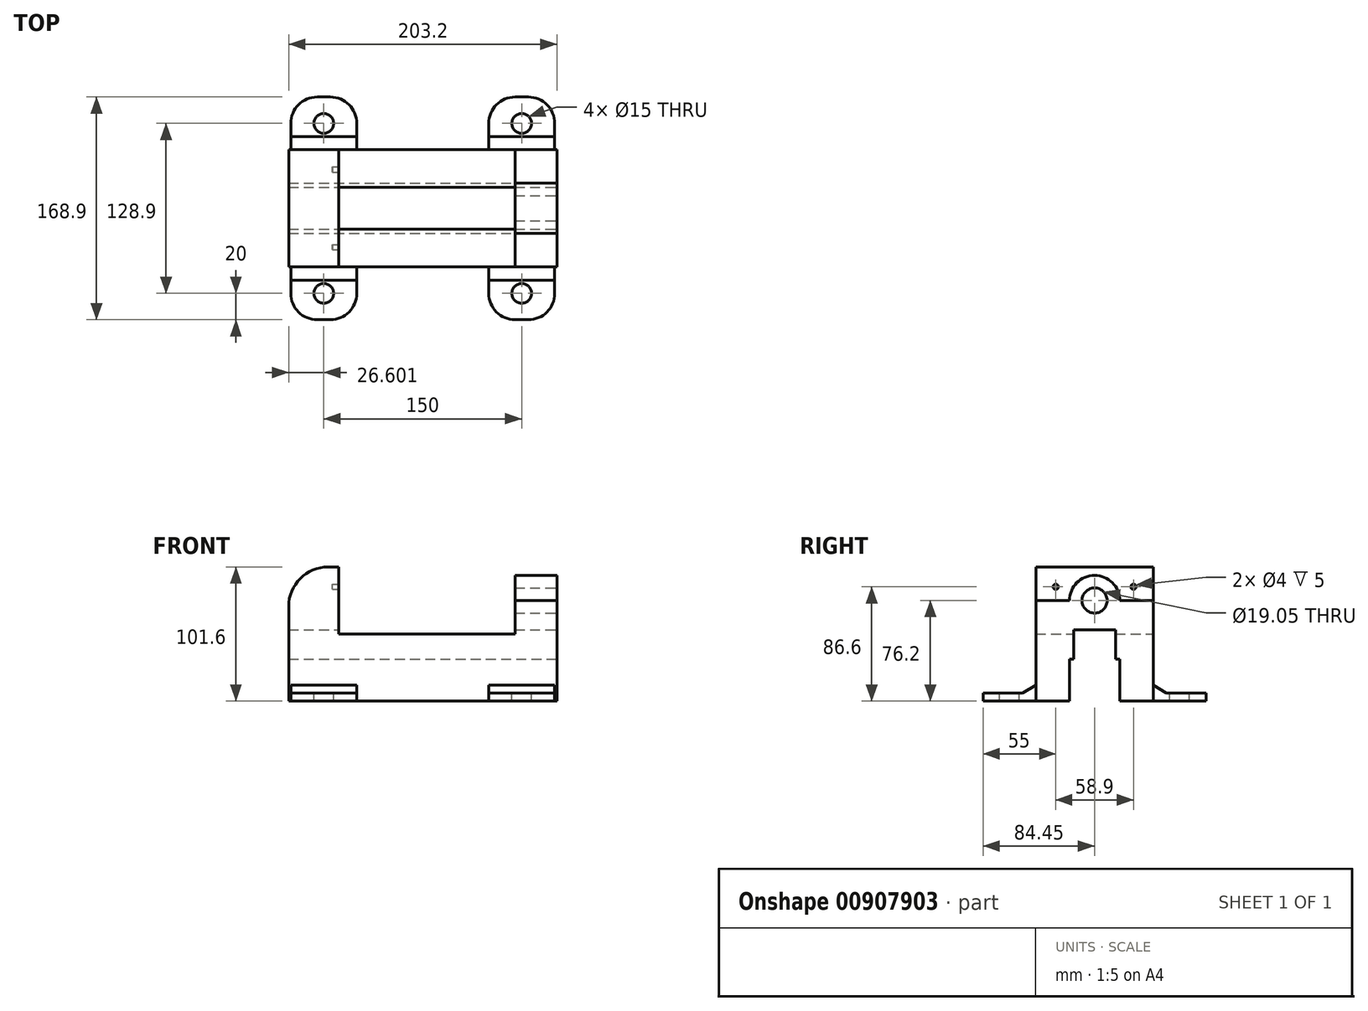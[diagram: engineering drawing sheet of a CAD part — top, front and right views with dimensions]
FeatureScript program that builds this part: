
annotation { "Feature Type Name" : "Feature", "Feature Type Description" : "" }
export const myFeature = defineFeature(function(context is Context, id is Id, definition is map)
    precondition{}
    {
        {
            var Q0;
            Q0=qCreatedBy(makeId("Front.planeOp"),FACE);
            var sketch = newSketch(context, id + "F0", { "sketchPlane" : qUnion([Q0])});
            skLineSegment(sketch, "E0", {"start": v(-86.38, 0) * mm, "end": v(116.82, 0) * mm});
            skLineSegment(sketch, "E1", {"start": v(116.82, 0) * mm, "end": v(116.82, 76.2) * mm});
            skLineSegment(sketch, "E2", {"start": v(116.82, 76.2) * mm, "end": v(85.07, 76.2) * mm});
            skLineSegment(sketch, "E3", {"start": v(85.07, 76.2) * mm, "end": v(85.07, 50.8) * mm});
            skLineSegment(sketch, "E4", {"start": v(85.07, 50.8) * mm, "end": v(-48.28, 50.8) * mm});
            skLineSegment(sketch, "E5", {"start": v(-48.28, 50.8) * mm, "end": v(-48.28, 101.6) * mm});
            skLineSegment(sketch, "E6", {"start": v(-48.28, 101.6) * mm, "end": v(-86.38, 101.6) * mm});
            skLineSegment(sketch, "E7", {"start": v(-86.38, 101.6) * mm, "end": v(-86.38, 0) * mm});
            skSolve(sketch);
        }
        {
            var Q0;
            Q0=makeQuery(id+"F0.imprint","IMPRINT",FACE,{"disambiguationData":[TD([[makeQuery(id+"F0.imprint","IMPRINT",EDGE,{"derivedFrom":sQuery(id+"F0.wireOp",EDGE,"E0")}),1.0]])]});
            extrude(context, id + "F1", {"entities" : qUnion([Q0]), "depth" : 88.9 * mm, "offsetDistance" : 25 * mm});
        }
        {
            var Q0;
            Q0=makeQuery(id+"F1.opExtrude","SWEPT_EDGE",EDGE,{"disambiguationData":[OSD([sQuery(id+"F0.wireOp",EDGE,"E6"),sQuery(id+"F0.wireOp",EDGE,"E7")])]});
            fillet(context, id + "F2", {"entities" : qUnion([Q0]), "radius" : 30 * mm, "tangentPropagation" : true, "allowEdgeOverflow" : false});
        }
        {
            var Q0;
            Q0=makeQuery(id+"F1.opExtrude","SWEPT_FACE",FACE,{"disambiguationData":[OSD([sQuery(id+"F0.wireOp",EDGE,"E1")])]});
            var sketch = newSketch(context, id + "F3", { "sketchPlane" : qUnion([Q0])});
            skCircle(sketch, "E8", {"center": v(-44.45, 76.2) * mm, "radius": 19.05 * mm});
            skSolve(sketch);
        }
        {
            var Q0;
            {var subQ0=sQuery(id+"F3.wireOp",EDGE,"E8");var subQ1=makeQuery(id+"F1.opExtrude","SWEPT_EDGE",EDGE,{"disambiguationData":[OSD([sQuery(id+"F0.wireOp",EDGE,"E1"),sQuery(id+"F0.wireOp",EDGE,"E2")])]});var subQ2=makeQuery(id+"F3.imprint","INTERSECT",VERTEX,{"disambiguationData":[OD(0.0)],"derivedFrom":[subQ1,subQ0]});Q0=makeQuery(id+"F3.imprint","IMPRINT",FACE,{"disambiguationData":[TD([[makeQuery(id+"F3.imprint","IMPRINT",EDGE,{"disambiguationData":[TD([[subQ2,-1.0]])],"derivedFrom":subQ0}),1.0]])]});}
            extrude(context, id + "F4", {"entities" : qUnion([Q0]), "operationType" : NewBodyOperationType.ADD, "oppositeDirection" : true, "depth" : 31.75 * mm, "offsetDistance" : 25 * mm});
        }
        {
            var Q0;
            {var subQ0=sQuery(id+"F0.wireOp",EDGE,"E1");Q0=makeQuery(id+"F4.boolean.opBoolean","MERGE",FACE,{"derivedFrom":[makeQuery(id+"F1.opExtrude","SWEPT_FACE",FACE,{"disambiguationData":[OSD([subQ0])]}),makeQuery(id+"F4.opExtrude","CAP_FACE",FACE,{"disambiguationData":[OSD([subQ0,sQuery(id+"F0.wireOp",EDGE,"E2"),sQuery(id+"F3.wireOp",EDGE,"E8")])],"isStart":true})]});}
            var sketch = newSketch(context, id + "F5", { "sketchPlane" : qUnion([Q0])});
            skCircle(sketch, "E9", {"center": v(-44.45, 76.2) * mm, "radius": 19.05 * mm});
            skCircle(sketch, "E10", {"center": v(-44.45, 76.2) * mm, "radius": 7.94 * mm});
            skSolve(sketch);
        }
        {
            var Q0;
            Q0=makeQuery(id+"F5.imprint","IMPRINT",FACE,{"disambiguationData":[TD([[makeQuery(id+"F5.imprint","IMPRINT",EDGE,{"derivedFrom":sQuery(id+"F5.wireOp",EDGE,"E10")}),1.0]])]});
            extrude(context, id + "F6", {"entities" : qUnion([Q0]), "operationType" : NewBodyOperationType.REMOVE, "oppositeDirection" : true, "depth" : 55 * mm, "offsetDistance" : 25 * mm});
        }
        {
            var Q0;
            {var subQ0=sQuery(id+"F0.wireOp",EDGE,"E1");Q0=makeQuery(id+"F4.boolean.opBoolean","MERGE",FACE,{"derivedFrom":[makeQuery(id+"F1.opExtrude","SWEPT_FACE",FACE,{"disambiguationData":[OSD([subQ0])]}),makeQuery(id+"F4.opExtrude","CAP_FACE",FACE,{"disambiguationData":[OSD([subQ0,sQuery(id+"F0.wireOp",EDGE,"E2"),sQuery(id+"F3.wireOp",EDGE,"E8")])],"isStart":true})]});}
            var sketch = newSketch(context, id + "F7", { "sketchPlane" : qUnion([Q0])});
            skLineSegment(sketch, "E11", {"start": v(-44.45, 0) * mm, "end": v(-63.5, 0) * mm});
            skLineSegment(sketch, "E12", {"start": v(-63.5, 0) * mm, "end": v(-25.4, 0) * mm});
            skLineSegment(sketch, "E13", {"start": v(-25.4, 0) * mm, "end": v(-25.4, 31.75) * mm});
            skLineSegment(sketch, "E14", {"start": v(-25.4, 31.75) * mm, "end": v(-63.5, 31.75) * mm});
            skLineSegment(sketch, "E15", {"start": v(-63.5, 31.75) * mm, "end": v(-63.5, 0) * mm});
            skLineSegment(sketch, "E16", {"start": v(-44.45, 31.75) * mm, "end": v(-44.45, 53.98) * mm});
            skLineSegment(sketch, "E17", {"start": v(-44.45, 53.98) * mm, "end": v(-60.33, 53.98) * mm});
            skLineSegment(sketch, "E18", {"start": v(-60.33, 53.98) * mm, "end": v(-60.33, 31.75) * mm});
            skLineSegment(sketch, "E19", {"start": v(-60.33, 31.75) * mm, "end": v(-28.57, 31.75) * mm});
            skLineSegment(sketch, "E20", {"start": v(-28.57, 31.75) * mm, "end": v(-28.57, 53.98) * mm});
            skLineSegment(sketch, "E21", {"start": v(-28.57, 53.98) * mm, "end": v(-44.45, 53.98) * mm});
            skSolve(sketch);
        }
        {
            var Q0;
            {var subQ4=sQuery(id+"F7.wireOp",EDGE,"E13");Q0=makeQuery(id+"F7.imprint","IMPRINT",FACE,{"disambiguationData":[TD([[makeQuery(id+"F7.imprint","IMPRINT",EDGE,{"derivedFrom":subQ4}),1.0]])]});}
            var Q1;
            {var subQ0=sQuery(id+"F7.wireOp",EDGE,"E16");Q1=makeQuery(id+"F7.imprint","IMPRINT",FACE,{"disambiguationData":[TD([[makeQuery(id+"F7.imprint","IMPRINT",EDGE,{"derivedFrom":subQ0}),1.0]])]});}
            var Q2;
            {var subQ0=sQuery(id+"F7.wireOp",EDGE,"E16");Q2=makeQuery(id+"F7.imprint","IMPRINT",FACE,{"disambiguationData":[TD([[makeQuery(id+"F7.imprint","IMPRINT",EDGE,{"derivedFrom":subQ0}),-1.0]])]});}
            extrude(context, id + "F8", {"entities" : qUnion([Q0, Q1, Q2]), "operationType" : NewBodyOperationType.REMOVE, "oppositeDirection" : true, "depth" : 265 * mm, "offsetDistance" : 25 * mm});
        }
        {
            var Q0;
            Q0=makeQuery(id+"F1.opExtrude","CAP_FACE",FACE,{"disambiguationData":[OSD([sQuery(id+"F0.wireOp",EDGE,"E0"),sQuery(id+"F0.wireOp",EDGE,"E1"),sQuery(id+"F0.wireOp",EDGE,"E2"),sQuery(id+"F0.wireOp",EDGE,"E3"),sQuery(id+"F0.wireOp",EDGE,"E4"),sQuery(id+"F0.wireOp",EDGE,"E5"),sQuery(id+"F0.wireOp",EDGE,"E6"),sQuery(id+"F0.wireOp",EDGE,"E7")])],"isStart":false});
            var sketch = newSketch(context, id + "F9", { "sketchPlane" : qUnion([Q0])});
            skLineSegment(sketch, "E22", {"start": v(-86.38, 0) * mm, "end": v(-84.78, 0) * mm});
            skLineSegment(sketch, "E23", {"start": v(-84.78, 0) * mm, "end": v(-84.78, 6) * mm});
            skLineSegment(sketch, "E24", {"start": v(-84.78, 6) * mm, "end": v(-34.78, 6) * mm});
            skLineSegment(sketch, "E25", {"start": v(-34.78, 6) * mm, "end": v(-34.78, 0) * mm});
            skLineSegment(sketch, "E26", {"start": v(-34.78, 0) * mm, "end": v(-84.78, 0) * mm});
            skLineSegment(sketch, "E27", {"start": v(116.82, 0) * mm, "end": v(115.22, 0) * mm});
            skLineSegment(sketch, "E28", {"start": v(115.22, 0) * mm, "end": v(115.22, 6) * mm});
            skLineSegment(sketch, "E29", {"start": v(115.22, 6) * mm, "end": v(65.22, 6) * mm});
            skLineSegment(sketch, "E30", {"start": v(65.22, 6) * mm, "end": v(65.22, 0) * mm});
            skLineSegment(sketch, "E31", {"start": v(65.22, 0) * mm, "end": v(115.22, 0) * mm});
            skSolve(sketch);
        }
        {
            var Q0;
            Q0=makeQuery(id+"F9.imprint","IMPRINT",FACE,{"disambiguationData":[TD([[makeQuery(id+"F9.imprint","IMPRINT",EDGE,{"derivedFrom":sQuery(id+"F9.wireOp",EDGE,"E23")}),-1.0]])]});
            var Q1;
            Q1=makeQuery(id+"F9.imprint","IMPRINT",FACE,{"disambiguationData":[TD([[makeQuery(id+"F9.imprint","IMPRINT",EDGE,{"derivedFrom":sQuery(id+"F9.wireOp",EDGE,"E28")}),1.0]])]});
            extrude(context, id + "F10", {"entities" : qUnion([Q0, Q1]), "operationType" : NewBodyOperationType.ADD, "depth" : 40 * mm, "offsetDistance" : 25 * mm});
        }
        {
            var Q0;
            Q0=makeQuery(id+"F10.opExtrude","CAP_EDGE",EDGE,{"disambiguationData":[OSD([sQuery(id+"F9.wireOp",EDGE,"E23")])],"isStart":false});
            var Q1;
            Q1=makeQuery(id+"F10.opExtrude","CAP_EDGE",EDGE,{"disambiguationData":[OSD([sQuery(id+"F9.wireOp",EDGE,"E25")])],"isStart":false});
            var Q2;
            Q2=makeQuery(id+"F10.opExtrude","CAP_EDGE",EDGE,{"disambiguationData":[OSD([sQuery(id+"F9.wireOp",EDGE,"E30")])],"isStart":false});
            var Q3;
            Q3=makeQuery(id+"F10.opExtrude","CAP_EDGE",EDGE,{"disambiguationData":[OSD([sQuery(id+"F9.wireOp",EDGE,"E28")])],"isStart":false});
            fillet(context, id + "F11", {"entities" : qUnion([Q0, Q1, Q2, Q3]), "radius" : 20 * mm, "tangentPropagation" : true, "allowEdgeOverflow" : false});
        }
        {
            var Q0;
            Q0=makeQuery(id+"F1.opExtrude","CAP_FACE",FACE,{"disambiguationData":[OSD([sQuery(id+"F0.wireOp",EDGE,"E0"),sQuery(id+"F0.wireOp",EDGE,"E1"),sQuery(id+"F0.wireOp",EDGE,"E2"),sQuery(id+"F0.wireOp",EDGE,"E3"),sQuery(id+"F0.wireOp",EDGE,"E4"),sQuery(id+"F0.wireOp",EDGE,"E5"),sQuery(id+"F0.wireOp",EDGE,"E6"),sQuery(id+"F0.wireOp",EDGE,"E7")])],"isStart":true});
            var sketch = newSketch(context, id + "F12", { "sketchPlane" : qUnion([Q0])});
            skLineSegment(sketch, "E32", {"start": v(-116.82, 0) * mm, "end": v(-115.22, 0) * mm});
            skLineSegment(sketch, "E33", {"start": v(-115.22, 0) * mm, "end": v(-115.22, 6) * mm});
            skLineSegment(sketch, "E34", {"start": v(-115.22, 6) * mm, "end": v(-65.22, 6) * mm});
            skLineSegment(sketch, "E35", {"start": v(-65.22, 6) * mm, "end": v(-65.22, 0) * mm});
            skLineSegment(sketch, "E36", {"start": v(-65.22, 0) * mm, "end": v(-115.22, 0) * mm});
            skLineSegment(sketch, "E37", {"start": v(86.38, 0) * mm, "end": v(84.78, 0) * mm});
            skLineSegment(sketch, "E38", {"start": v(84.78, 0) * mm, "end": v(84.78, 6) * mm});
            skLineSegment(sketch, "E39", {"start": v(84.78, 6) * mm, "end": v(34.78, 6) * mm});
            skLineSegment(sketch, "E40", {"start": v(34.78, 6) * mm, "end": v(34.78, 0) * mm});
            skLineSegment(sketch, "E41", {"start": v(34.78, 0) * mm, "end": v(84.78, 0) * mm});
            skSolve(sketch);
        }
        {
            var Q0;
            Q0=makeQuery(id+"F12.imprint","IMPRINT",FACE,{"disambiguationData":[TD([[makeQuery(id+"F12.imprint","IMPRINT",EDGE,{"derivedFrom":sQuery(id+"F12.wireOp",EDGE,"E33")}),-1.0]])]});
            var Q1;
            Q1=makeQuery(id+"F12.imprint","IMPRINT",FACE,{"disambiguationData":[TD([[makeQuery(id+"F12.imprint","IMPRINT",EDGE,{"derivedFrom":sQuery(id+"F12.wireOp",EDGE,"E38")}),1.0]])]});
            extrude(context, id + "F13", {"entities" : qUnion([Q0, Q1]), "operationType" : NewBodyOperationType.ADD, "depth" : 40 * mm, "offsetDistance" : 25 * mm});
        }
        {
            var Q0;
            Q0=makeQuery(id+"F13.opExtrude","CAP_EDGE",EDGE,{"disambiguationData":[OSD([sQuery(id+"F12.wireOp",EDGE,"E33")])],"isStart":false});
            var Q1;
            Q1=makeQuery(id+"F13.opExtrude","CAP_EDGE",EDGE,{"disambiguationData":[OSD([sQuery(id+"F12.wireOp",EDGE,"E35")])],"isStart":false});
            var Q2;
            Q2=makeQuery(id+"F13.opExtrude","CAP_EDGE",EDGE,{"disambiguationData":[OSD([sQuery(id+"F12.wireOp",EDGE,"E40")])],"isStart":false});
            var Q3;
            Q3=makeQuery(id+"F13.opExtrude","CAP_EDGE",EDGE,{"disambiguationData":[OSD([sQuery(id+"F12.wireOp",EDGE,"E38")])],"isStart":false});
            fillet(context, id + "F14", {"entities" : qUnion([Q0, Q1, Q2, Q3]), "radius" : 20 * mm, "tangentPropagation" : true, "allowEdgeOverflow" : false});
        }
        {
            var Q0;
            Q0=makeQuery(id+"F13.opExtrude","SWEPT_FACE",FACE,{"disambiguationData":[OSD([sQuery(id+"F12.wireOp",EDGE,"E34")])]});
            var sketch = newSketch(context, id + "F15", { "sketchPlane" : qUnion([Q0])});
            skLineSegment(sketch, "E42", {"start": v(90.22, 40) * mm, "end": v(90.22, 20) * mm});
            skCircle(sketch, "E43", {"center": v(90.22, 20) * mm, "radius": 7.5 * mm});
            skSolve(sketch);
        }
        {
            var Q0;
            Q0=makeQuery(id+"F15.imprint","IMPRINT",FACE,{"disambiguationData":[TD([[makeQuery(id+"F15.imprint","IMPRINT",EDGE,{"derivedFrom":sQuery(id+"F15.wireOp",EDGE,"E43")}),1.0]])]});
            extrude(context, id + "F16", {"entities" : qUnion([Q0]), "operationType" : NewBodyOperationType.REMOVE, "oppositeDirection" : true, "depth" : 25 * mm, "offsetDistance" : 25 * mm});
        }
        {
            var Q0;
            Q0=makeQuery(id+"F13.opExtrude","SWEPT_FACE",FACE,{"disambiguationData":[OSD([sQuery(id+"F12.wireOp",EDGE,"E39")])]});
            var sketch = newSketch(context, id + "F17", { "sketchPlane" : qUnion([Q0])});
            skLineSegment(sketch, "E44", {"start": v(-59.78, 40) * mm, "end": v(-59.78, 20) * mm});
            skCircle(sketch, "E45", {"center": v(-59.78, 20) * mm, "radius": 7.5 * mm});
            skSolve(sketch);
        }
        {
            var Q0;
            Q0=makeQuery(id+"F17.imprint","IMPRINT",FACE,{"disambiguationData":[TD([[makeQuery(id+"F17.imprint","IMPRINT",EDGE,{"derivedFrom":sQuery(id+"F17.wireOp",EDGE,"E45")}),1.0]])]});
            extrude(context, id + "F18", {"entities" : qUnion([Q0]), "operationType" : NewBodyOperationType.REMOVE, "oppositeDirection" : true, "depth" : 25 * mm, "offsetDistance" : 25 * mm});
        }
        {
            var Q0;
            Q0=makeQuery(id+"F10.opExtrude","SWEPT_FACE",FACE,{"disambiguationData":[OSD([sQuery(id+"F9.wireOp",EDGE,"E24")])]});
            var sketch = newSketch(context, id + "F19", { "sketchPlane" : qUnion([Q0])});
            skLineSegment(sketch, "E46", {"start": v(-59.78, -128.9) * mm, "end": v(-59.78, -108.9) * mm});
            skCircle(sketch, "E47", {"center": v(-59.78, -108.9) * mm, "radius": 7.5 * mm});
            skSolve(sketch);
        }
        {
            var Q0;
            Q0=makeQuery(id+"F19.imprint","IMPRINT",FACE,{"disambiguationData":[TD([[makeQuery(id+"F19.imprint","IMPRINT",EDGE,{"derivedFrom":sQuery(id+"F19.wireOp",EDGE,"E47")}),1.0]])]});
            extrude(context, id + "F20", {"entities" : qUnion([Q0]), "operationType" : NewBodyOperationType.REMOVE, "oppositeDirection" : true, "depth" : 25 * mm, "offsetDistance" : 25 * mm});
        }
        {
            var Q0;
            Q0=makeQuery(id+"F10.opExtrude","SWEPT_FACE",FACE,{"disambiguationData":[OSD([sQuery(id+"F9.wireOp",EDGE,"E29")])]});
            var sketch = newSketch(context, id + "F21", { "sketchPlane" : qUnion([Q0])});
            skLineSegment(sketch, "E48", {"start": v(90.22, -128.9) * mm, "end": v(90.22, -108.9) * mm});
            skCircle(sketch, "E49", {"center": v(90.22, -108.9) * mm, "radius": 7.5 * mm});
            skSolve(sketch);
        }
        {
            var Q0;
            Q0=makeQuery(id+"F21.imprint","IMPRINT",FACE,{"disambiguationData":[TD([[makeQuery(id+"F21.imprint","IMPRINT",EDGE,{"derivedFrom":sQuery(id+"F21.wireOp",EDGE,"E49")}),1.0]])]});
            extrude(context, id + "F22", {"entities" : qUnion([Q0]), "operationType" : NewBodyOperationType.REMOVE, "oppositeDirection" : true, "depth" : 25 * mm, "offsetDistance" : 25 * mm});
        }
        {
            var Q0;
            Q0=makeQuery(id+"F10.opExtrude","SWEPT_FACE",FACE,{"disambiguationData":[OSD([sQuery(id+"F9.wireOp",EDGE,"E23")])]});
            var sketch = newSketch(context, id + "F23", { "sketchPlane" : qUnion([Q0])});
            skLineSegment(sketch, "E50", {"start": v(98.9, 6) * mm, "end": v(88.9, 6) * mm});
            skLineSegment(sketch, "E51", {"start": v(88.9, 6) * mm, "end": v(88.9, 12) * mm});
            skLineSegment(sketch, "E52", {"start": v(88.9, 12) * mm, "end": v(98.9, 6) * mm});
            skSolve(sketch);
        }
        {
            var Q0;
            Q0=makeQuery(id+"F23.imprint","IMPRINT",FACE,{"disambiguationData":[TD([[makeQuery(id+"F23.imprint","IMPRINT",EDGE,{"derivedFrom":sQuery(id+"F23.wireOp",EDGE,"E50")}),-1.0]])]});
            extrude(context, id + "F24", {"entities" : qUnion([Q0]), "operationType" : NewBodyOperationType.ADD, "oppositeDirection" : true, "depth" : 50 * mm, "offsetDistance" : 25 * mm});
        }
        {
            var Q0;
            Q0=makeQuery(id+"F10.opExtrude","SWEPT_FACE",FACE,{"disambiguationData":[OSD([sQuery(id+"F9.wireOp",EDGE,"E28")])]});
            var sketch = newSketch(context, id + "F25", { "sketchPlane" : qUnion([Q0])});
            skLineSegment(sketch, "E53", {"start": v(-98.9, 6) * mm, "end": v(-88.9, 6) * mm});
            skLineSegment(sketch, "E54", {"start": v(-88.9, 6) * mm, "end": v(-88.9, 12) * mm});
            skLineSegment(sketch, "E55", {"start": v(-88.9, 12) * mm, "end": v(-98.9, 6) * mm});
            skSolve(sketch);
        }
        {
            var Q0;
            Q0=makeQuery(id+"F25.imprint","IMPRINT",FACE,{"disambiguationData":[TD([[makeQuery(id+"F25.imprint","IMPRINT",EDGE,{"derivedFrom":sQuery(id+"F25.wireOp",EDGE,"E53")}),1.0]])]});
            extrude(context, id + "F26", {"entities" : qUnion([Q0]), "operationType" : NewBodyOperationType.ADD, "oppositeDirection" : true, "depth" : 50 * mm, "offsetDistance" : 25 * mm});
        }
        {
            var Q0;
            Q0=makeQuery(id+"F13.opExtrude","SWEPT_FACE",FACE,{"disambiguationData":[OSD([sQuery(id+"F12.wireOp",EDGE,"E33")])]});
            var sketch = newSketch(context, id + "F27", { "sketchPlane" : qUnion([Q0])});
            skLineSegment(sketch, "E56", {"start": v(10, 6) * mm, "end": v(0, 6) * mm});
            skLineSegment(sketch, "E57", {"start": v(0, 6) * mm, "end": v(0, 12) * mm});
            skLineSegment(sketch, "E58", {"start": v(0, 12) * mm, "end": v(10, 6) * mm});
            skSolve(sketch);
        }
        {
            var Q0;
            Q0=makeQuery(id+"F27.imprint","IMPRINT",FACE,{"disambiguationData":[TD([[makeQuery(id+"F27.imprint","IMPRINT",EDGE,{"derivedFrom":sQuery(id+"F27.wireOp",EDGE,"E56")}),-1.0]])]});
            extrude(context, id + "F28", {"entities" : qUnion([Q0]), "operationType" : NewBodyOperationType.ADD, "oppositeDirection" : true, "depth" : 50 * mm, "offsetDistance" : 25 * mm});
        }
        {
            var Q0;
            Q0=makeQuery(id+"F13.opExtrude","SWEPT_FACE",FACE,{"disambiguationData":[OSD([sQuery(id+"F12.wireOp",EDGE,"E38")])]});
            var sketch = newSketch(context, id + "F29", { "sketchPlane" : qUnion([Q0])});
            skLineSegment(sketch, "E59", {"start": v(-10, 6) * mm, "end": v(0, 6) * mm});
            skLineSegment(sketch, "E60", {"start": v(0, 6) * mm, "end": v(0, 12) * mm});
            skLineSegment(sketch, "E61", {"start": v(0, 12) * mm, "end": v(-10, 6) * mm});
            skSolve(sketch);
        }
        {
            var Q0;
            Q0=makeQuery(id+"F29.imprint","IMPRINT",FACE,{"disambiguationData":[TD([[makeQuery(id+"F29.imprint","IMPRINT",EDGE,{"derivedFrom":sQuery(id+"F29.wireOp",EDGE,"E59")}),1.0]])]});
            extrude(context, id + "F30", {"entities" : qUnion([Q0]), "operationType" : NewBodyOperationType.ADD, "oppositeDirection" : true, "depth" : 50 * mm, "offsetDistance" : 25 * mm});
        }
        {
            var Q0;
            Q0=makeQuery(id+"F1.opExtrude","SWEPT_FACE",FACE,{"disambiguationData":[OSD([sQuery(id+"F0.wireOp",EDGE,"E5")])]});
            var sketch = newSketch(context, id + "F31", { "sketchPlane" : qUnion([Q0])});
            skLineSegment(sketch, "E62", {"start": v(-88.9, 101.6) * mm, "end": v(-88.9, 86.6) * mm});
            skLineSegment(sketch, "E63", {"start": v(-88.9, 86.6) * mm, "end": v(-73.9, 86.6) * mm});
            skCircle(sketch, "E64", {"center": v(-73.9, 86.6) * mm, "radius": 2 * mm});
            skLineSegment(sketch, "E65", {"start": v(0, 101.6) * mm, "end": v(0, 86.6) * mm});
            skLineSegment(sketch, "E66", {"start": v(0, 86.6) * mm, "end": v(-15, 86.6) * mm});
            skCircle(sketch, "E67", {"center": v(-15, 86.6) * mm, "radius": 2 * mm});
            skSolve(sketch);
        }
        {
            var Q0;
            Q0=makeQuery(id+"F31.imprint","IMPRINT",FACE,{"disambiguationData":[TD([[makeQuery(id+"F31.imprint","IMPRINT",EDGE,{"derivedFrom":sQuery(id+"F31.wireOp",EDGE,"E64")}),1.0]])]});
            var Q1;
            Q1=makeQuery(id+"F31.imprint","IMPRINT",FACE,{"disambiguationData":[TD([[makeQuery(id+"F31.imprint","IMPRINT",EDGE,{"derivedFrom":sQuery(id+"F31.wireOp",EDGE,"E67")}),1.0]])]});
            extrude(context, id + "F32", {"entities" : qUnion([Q0, Q1]), "operationType" : NewBodyOperationType.REMOVE, "oppositeDirection" : true, "depth" : 5 * mm, "offsetDistance" : 25 * mm});
        }
        {
            var Q0;
            {var subQ0=sQuery(id+"F0.wireOp",EDGE,"E1");Q0=makeQuery(id+"F4.boolean.opBoolean","MERGE",FACE,{"derivedFrom":[makeQuery(id+"F1.opExtrude","SWEPT_FACE",FACE,{"disambiguationData":[OSD([subQ0])]}),makeQuery(id+"F4.opExtrude","CAP_FACE",FACE,{"disambiguationData":[OSD([subQ0,sQuery(id+"F0.wireOp",EDGE,"E2"),sQuery(id+"F3.wireOp",EDGE,"E8")])],"isStart":true})]});}
            var sketch = newSketch(context, id + "F33", { "sketchPlane" : qUnion([Q0])});
            skCircle(sketch, "E68", {"center": v(-44.45, 76.2) * mm, "radius": 9.53 * mm});
            skSolve(sketch);
        }
        {
            var Q0;
            Q0=makeQuery(id+"F33.imprint","IMPRINT",FACE,{"disambiguationData":[TD([[makeQuery(id+"F33.imprint","IMPRINT",EDGE,{"derivedFrom":sQuery(id+"F33.wireOp",EDGE,"E68")}),1.0]])]});
            extrude(context, id + "F34", {"entities" : qUnion([Q0]), "operationType" : NewBodyOperationType.REMOVE, "oppositeDirection" : true, "depth" : 78.1 * mm, "offsetDistance" : 25 * mm});
        }
    });
